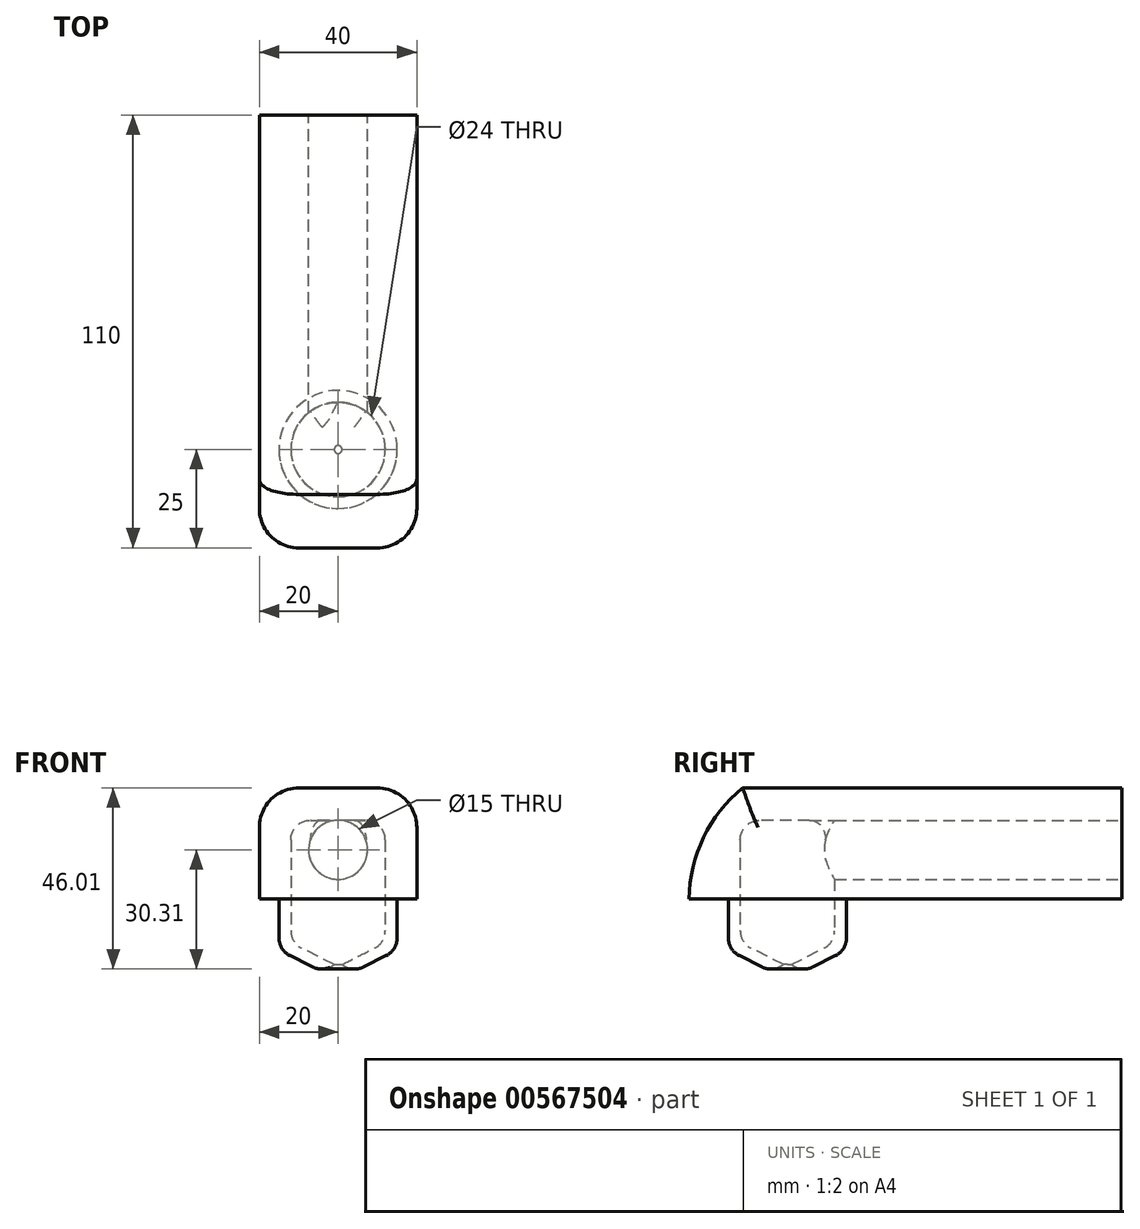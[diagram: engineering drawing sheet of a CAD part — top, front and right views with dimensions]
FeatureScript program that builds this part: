
annotation { "Feature Type Name" : "Feature", "Feature Type Description" : "" }
export const myFeature = defineFeature(function(context is Context, id is Id, definition is map)
    precondition{}
    {
        {
            var Q0;
            Q0=qCreatedBy(makeId("Right.planeOp"),FACE);
            var sketch = newSketch(context, id + "F0", { "sketchPlane" : qUnion([Q0])});
            skLineSegment(sketch, "E0", {"start": v(-15, 20) * mm, "end": v(-15, 7) * mm});
            skLineSegment(sketch, "E1", {"start": v(-15, 7) * mm, "end": v(-1, 0) * mm});
            skLineSegment(sketch, "E2.0", {"start": v(-12, 8.85) * mm, "end": v(-1, 3.35) * mm});
            skLineSegment(sketch, "E2.1", {"start": v(-12, 20) * mm, "end": v(-12, 8.85) * mm});
            skLineSegment(sketch, "E3", {"start": v(-15, 20) * mm, "end": v(-12, 20) * mm});
            skLineSegment(sketch, "E4", {"start": v(-1, 0) * mm, "end": v(-1, 3.35) * mm});
            skSolve(sketch);
        }
        {
            var Q0;
            Q0=qCreatedBy(makeId("Right.planeOp"),FACE);
            var sketch = newSketch(context, id + "F1", { "sketchPlane" : qUnion([Q0])});
            skLineSegment(sketch, "E5", {"start": v(0, -9) * mm, "end": v(0, 56.22) * mm, "construction": true});
            skSolve(sketch);
        }
        {
            var Q0;
            Q0=makeQuery(id+"F0.imprint","IMPRINT",FACE,{"disambiguationData":[TD([[makeQuery(id+"F0.imprint","IMPRINT",EDGE,{"derivedFrom":sQuery(id+"F0.wireOp",EDGE,"E0")}),1.0]])]});
            var Q1;
            Q1=sQuery(id+"F1.wireOp",EDGE,"E5");
            revolve(context, id + "F2", {"entities" : qUnion([Q0]), "axis" : qUnion([Q1]), "revolveType" : RevolveType.FULL});
        }
        {
            var Q0;
            Q0=makeQuery(id+"F2.opRevolve","SWEPT_EDGE",EDGE,{"disambiguationData":[OSD([sQuery(id+"F0.wireOp",EDGE,"E1"),sQuery(id+"F0.wireOp",EDGE,"E4")])]});
            fillet(context, id + "F3", {"entities" : qUnion([Q0]), "radius" : 5 * mm, "tangentPropagation" : true, "allowEdgeOverflow" : false});
        }
        {
            var Q0;
            Q0=makeQuery(id+"F2.opRevolve","SWEPT_EDGE",EDGE,{"disambiguationData":[OSD([sQuery(id+"F0.wireOp",EDGE,"E2.0"),sQuery(id+"F0.wireOp",EDGE,"E2.1")])]});
            var Q1;
            Q1=makeQuery(id+"F2.opRevolve","SWEPT_EDGE",EDGE,{"disambiguationData":[OSD([sQuery(id+"F0.wireOp",EDGE,"E0"),sQuery(id+"F0.wireOp",EDGE,"E1")])]});
            fillet(context, id + "F4", {"entities" : qUnion([Q0, Q1]), "radius" : 5 * mm, "tangentPropagation" : true, "allowEdgeOverflow" : false});
        }
        {
            var Q0;
            Q0=qCreatedBy(makeId("Right.planeOp"),FACE);
            var sketch = newSketch(context, id + "F5", { "sketchPlane" : qUnion([Q0])});
            skLineSegment(sketch, "E6", {"start": v(-15, 20) * mm, "end": v(-25, 20) * mm});
            skLineSegment(sketch, "E7", {"start": v(-15, 20) * mm, "end": v(85, 20) * mm});
            skArc(sketch, "E8", {"start": v(-11.4, 48.2) * mm, "mid": v(-21.32, 35.6) * mm, "end": v(-25, 20) * mm});
            skLineSegment(sketch, "E9", {"start": v(-11.4, 48.2) * mm, "end": v(85, 48.2) * mm});
            skLineSegment(sketch, "E10", {"start": v(85, 48.2) * mm, "end": v(85, 20) * mm});
            skSolve(sketch);
        }
        {
            var Q0;
            Q0 = qSketchRegion(id + "F5", true);
            extrude(context, id + "F6", {"entities" : qUnion([Q0]), "operationType" : NewBodyOperationType.ADD, "depth" : 20 * mm, "offsetDistance" : 25 * mm, "hasSecondDirection" : true, "secondDirectionOppositeDirection" : true, "secondDirectionDepth" : 20 * mm});
        }
        {
            var Q0;
            Q0=qCreatedBy(makeId("Right.planeOp"),FACE);
            var sketch = newSketch(context, id + "F7", { "sketchPlane" : qUnion([Q0])});
            skLineSegment(sketch, "E11", {"start": v(0, 0) * mm, "end": v(0, 20) * mm, "construction": true});
            skLineSegment(sketch, "E12", {"start": v(0, 20) * mm, "end": v(-12, 20) * mm});
            skLineSegment(sketch, "E13", {"start": v(-12, 20) * mm, "end": v(-12, 40) * mm});
            skLineSegment(sketch, "E14", {"start": v(-12, 40) * mm, "end": v(0, 40) * mm});
            skLineSegment(sketch, "E15", {"start": v(0, 40) * mm, "end": v(0, 20) * mm});
            skSolve(sketch);
        }
        {
            var Q0;
            Q0=qCreatedBy(makeId("Right.planeOp"),FACE);
            var sketch = newSketch(context, id + "F8", { "sketchPlane" : qUnion([Q0])});
            skLineSegment(sketch, "E16", {"start": v(0, 0) * mm, "end": v(0, 48.03) * mm, "construction": true});
            skSolve(sketch);
        }
        {
            var Q0;
            Q0 = qSketchRegion(id + "F7", true);
            var Q1;
            Q1=sQuery(id+"F8.wireOp",EDGE,"E16");
            revolve(context, id + "F9", {"operationType" : NewBodyOperationType.REMOVE, "entities" : qUnion([Q0]), "axis" : qUnion([Q1]), "revolveType" : RevolveType.FULL, "oppositeDirection" : true});
        }
        {
            var Q0;
            Q0=qCreatedBy(makeId("Right.planeOp"),FACE);
            var sketch = newSketch(context, id + "F10", { "sketchPlane" : qUnion([Q0])});
            skLineSegment(sketch, "E17.bottom", {"start": v(91.3, 25) * mm, "end": v(0, 25) * mm});
            skLineSegment(sketch, "E17.top", {"start": v(91.3, 32.5) * mm, "end": v(0, 32.5) * mm});
            skLineSegment(sketch, "E17.left", {"start": v(91.3, 25) * mm, "end": v(91.3, 32.5) * mm});
            skLineSegment(sketch, "E17.right", {"start": v(0, 25) * mm, "end": v(0, 32.5) * mm});
            skSolve(sketch);
        }
        {
            var Q0;
            Q0=qCreatedBy(makeId("Right.planeOp"),FACE);
            var sketch = newSketch(context, id + "F11", { "sketchPlane" : qUnion([Q0])});
            skLineSegment(sketch, "E18", {"start": v(0, 32.5) * mm, "end": v(97.85, 32.5) * mm, "construction": true});
            skSolve(sketch);
        }
        {
            var Q0;
            Q0 = qSketchRegion(id + "F10", true);
            var Q1;
            Q1=sQuery(id+"F11.wireOp",EDGE,"E18");
            revolve(context, id + "F12", {"operationType" : NewBodyOperationType.REMOVE, "entities" : qUnion([Q0]), "axis" : qUnion([Q1]), "revolveType" : RevolveType.FULL, "oppositeDirection" : true});
        }
        {
            var Q0;
            Q0=makeQuery(id+"F6.opExtrude","CAP_EDGE",EDGE,{"disambiguationData":[OSD([sQuery(id+"F5.wireOp",EDGE,"E8")])],"isStart":true});
            var Q1;
            Q1=makeQuery(id+"F6.opExtrude","CAP_EDGE",EDGE,{"disambiguationData":[OSD([sQuery(id+"F5.wireOp",EDGE,"E8")])],"isStart":false});
            var Q2;
            Q2=makeQuery(id+"F6.opExtrude","CAP_EDGE",EDGE,{"disambiguationData":[OSD([sQuery(id+"F5.wireOp",EDGE,"E9")])],"isStart":false});
            var Q3;
            Q3=makeQuery(id+"F6.opExtrude","CAP_EDGE",EDGE,{"disambiguationData":[OSD([sQuery(id+"F5.wireOp",EDGE,"E9")])],"isStart":true});
            fillet(context, id + "F13", {"entities" : qUnion([Q0, Q1, Q2, Q3]), "radius" : 10 * mm, "tangentPropagation" : true, "allowEdgeOverflow" : false});
        }
        {
            var Q0;
            Q0=qCreatedBy(makeId("Right.planeOp"),FACE);
            var sketch = newSketch(context, id + "F14", { "sketchPlane" : qUnion([Q0])});
            skLineSegment(sketch, "E19.bottom", {"start": v(85.68, 57) * mm, "end": v(-41.47, 57) * mm});
            skLineSegment(sketch, "E19.top", {"start": v(85.68, 0) * mm, "end": v(-41.47, 0) * mm});
            skLineSegment(sketch, "E19.left", {"start": v(85.68, 57) * mm, "end": v(85.68, 0) * mm});
            skLineSegment(sketch, "E19.right", {"start": v(-41.47, 57) * mm, "end": v(-41.47, 0) * mm});
            skSolve(sketch);
        }
        {
            var Q0;
            Q0=makeQuery(id+"F9.boolean.opBoolean","COPY",EDGE,{"derivedFrom":makeQuery(id+"F9.opRevolve","SWEPT_EDGE",EDGE,{"disambiguationData":[OSD([sQuery(id+"F7.wireOp",EDGE,"E13"),sQuery(id+"F7.wireOp",EDGE,"E14")])]})});
            fillet(context, id + "F15", {"entities" : qUnion([Q0]), "radius" : 5 * mm, "tangentPropagation" : true, "allowEdgeOverflow" : false});
        }
    });
